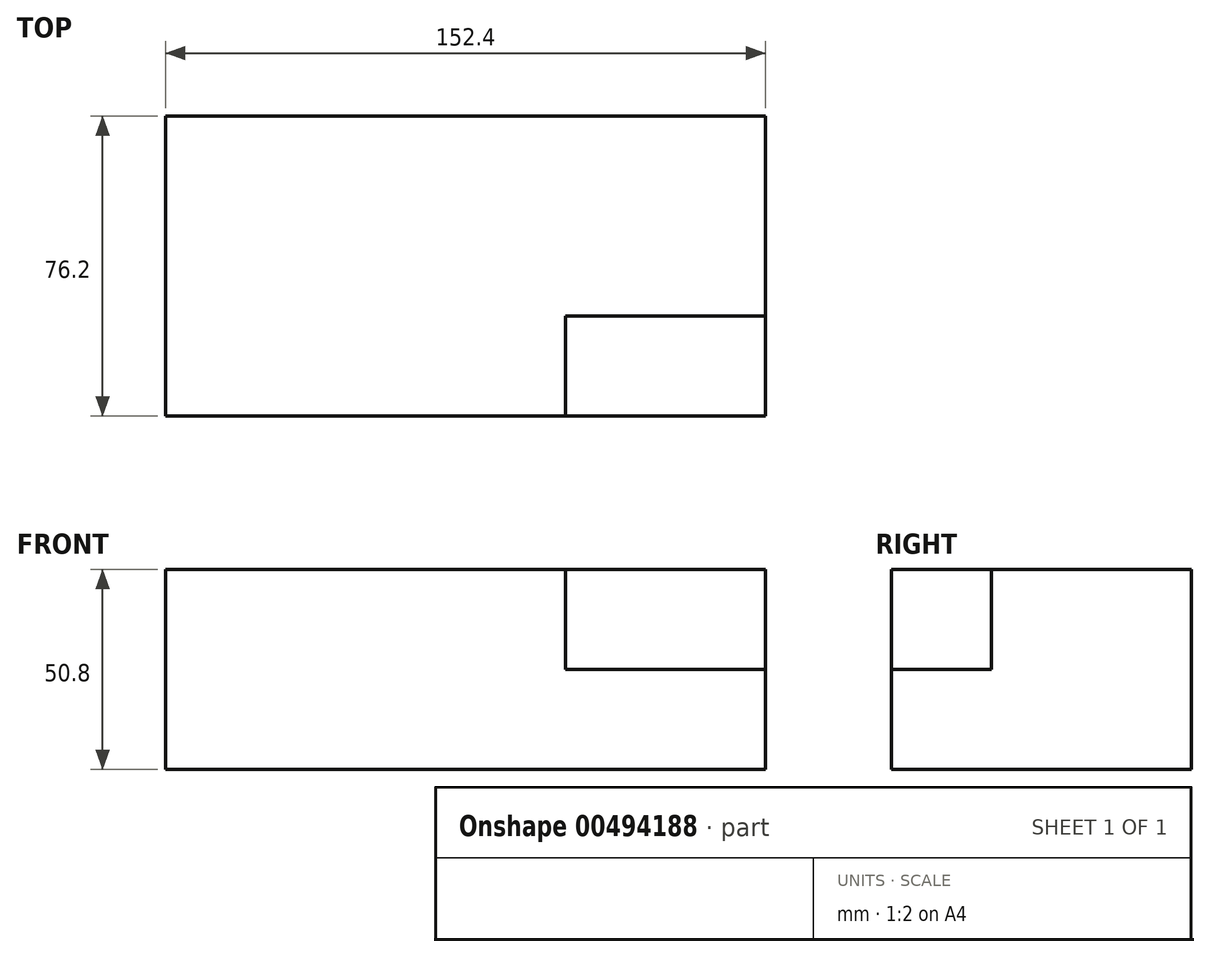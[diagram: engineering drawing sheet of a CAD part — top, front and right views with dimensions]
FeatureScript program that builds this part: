
annotation { "Feature Type Name" : "Feature", "Feature Type Description" : "" }
export const myFeature = defineFeature(function(context is Context, id is Id, definition is map)
    precondition{}
    {
        {
            var Q0;
            Q0=qCreatedBy(makeId("Top.planeOp"),FACE);
            var sketch = newSketch(context, id + "F0", { "sketchPlane" : qUnion([Q0])});
            skLineSegment(sketch, "E0.bottom", {"start": v(-77.84, 60.42) * mm, "end": v(74.56, 60.42) * mm});
            skLineSegment(sketch, "E0.top", {"start": v(-77.84, -15.78) * mm, "end": v(74.56, -15.78) * mm});
            skLineSegment(sketch, "E0.left", {"start": v(-77.84, 60.42) * mm, "end": v(-77.84, -15.78) * mm});
            skLineSegment(sketch, "E0.right", {"start": v(74.56, 60.42) * mm, "end": v(74.56, -15.78) * mm});
            skLineSegment(sketch, "E1.bottom", {"start": v(23.76, 9.62) * mm, "end": v(74.56, 9.62) * mm});
            skLineSegment(sketch, "E1.top", {"start": v(23.76, -15.78) * mm, "end": v(74.56, -15.78) * mm});
            skLineSegment(sketch, "E1.left", {"start": v(23.76, 9.62) * mm, "end": v(23.76, -15.78) * mm});
            skLineSegment(sketch, "E1.right", {"start": v(74.56, 9.62) * mm, "end": v(74.56, -15.78) * mm});
            skSolve(sketch);
        }
        {
            var Q0;
            Q0=makeQuery(id+"F0.imprint","IMPRINT",FACE,{"disambiguationData":[TD([[makeQuery(id+"F0.imprint","IMPRINT",EDGE,{"derivedFrom":sQuery(id+"F0.wireOp",EDGE,"E0.bottom")}),-1.0]])]});
            var Q1;
            Q1=makeQuery(id+"F0.imprint","IMPRINT",FACE,{"disambiguationData":[TD([[makeQuery(id+"F0.imprint","IMPRINT",EDGE,{"derivedFrom":sQuery(id+"F0.wireOp",EDGE,"E0.bottom")}),-1.0]])]});
            extrude(context, id + "F1", {"entities" : qUnion([Q0, Q1]), "depth" : 50.8 * mm});
        }
        {
            var Q0;
            Q0=makeQuery(id+"F0.imprint","IMPRINT",FACE,{"disambiguationData":[TD([[makeQuery(id+"F0.imprint","IMPRINT",EDGE,{"derivedFrom":sQuery(id+"F0.wireOp",EDGE,"E1.bottom")}),-1.0]])]});
            extrude(context, id + "F2", {"entities" : qUnion([Q0]), "operationType" : NewBodyOperationType.ADD, "depth" : 25.4 * mm});
        }
    });
